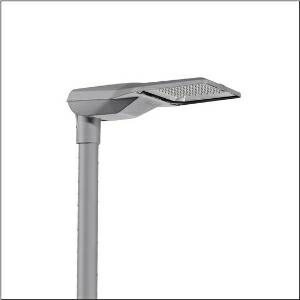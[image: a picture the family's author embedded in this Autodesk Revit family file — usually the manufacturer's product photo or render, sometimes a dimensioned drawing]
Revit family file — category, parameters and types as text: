
# Revit family: streetlight_sl_21_iq_midi___st1_5a_5xe3p41d08mb_62ad
name_source: partatom
category: Lighting Fixtures
units: mm (PartAtom-declared; Revit-internal decimal feet)

## family parameters
Cut with Voids When Loaded = No
Host = Face
Light Source = No
Part Type = Normal
Room Calculation Point = No
Round Connector Dimension = Use Diameter
Shared = No

## types (1)
- --- (1 x LED, 20000 lm, 146.7 W, 4000K)
    Apparent Load = 147 VA
    CIE Flux Codes = 22 53 95 100 100
    Color Rendering = 70
    Color Temperature = 4000K
    Default Elevation = 1800 mm
    Description = Streetlight SL 21 iQ midi, mast luminaire, primary light control with lens, of PMMA, primary optical cover: cover, of toughened safety glass, transparent, light distribution: ST1.5a, light emission: direct distribution, primary light characteristic: asymmetric, installation type: post-top, side-entry, LED, High Power LED, rated luminous flux: 20.000lm, luminous efficacy: 136lm/W, light colour: 740, colour temperature: 4000K, control gear: iQ-Comfort, control: Auto-Match, Temp-Guard, Lumen-Switch, Night-Set, Smart-Wire, Light-Fading, Desk-Remote (wireless, voltage-free reading and setting of iQ features in the workshop via application-optimized NFC function/RFID function), optimised constant luminous flux control (CLO 2.0), pre-setting: linear dimming characteristic, mains connection: 230..240V, AC, 50/60Hz, start of lifetime: 147W, end of service life: 161W, reduction: 62W, luminaire housing, of diecast aluminium, powder-coated, Siteco® metallic grey (DB 702S), corrosivity category C5 mid according to DIN EN ISO 12944, please order mast flange separately, inclination adjustable: 0°, 5°, 10°, 15°, sealing non-destructively replaceable, multi-level sealing system, length: 644mm, width: 335mm, height: 110mm, mast flange for spigot size: 42mm (side-entry): 5XC10008XM4, 60/48mm (side-entry/post-top): 5XC10108XM2, 76/60mm (side-entry/post-top): 5XC10108XM1, mounting height: 4..8m, protection rating (complete): IP66, insulation class (complete): insulation class II (safety insulation), certification: CE, ENEC, ENEC+, VDE, impact resistance: IK10, permissible operating ambient temperature for outdoor applications: -40..+50°C, standard-compliant lighting for roads and squares, packaging unit: 1 piece

Light Distribution: ST1.5a
    Height = 111 mm
    Lamp = 1 x LED
    Lamp Light Flux = 20000 lm
    Lamp Power = 146.7 W
    Lamp count = 1
    Length = 644 mm
    Luminous efficacy = 136 lm/W
    Manufacturer = Siteco
    ModVariant = No
    Model = 5XE3P41D08MB
    Number of Poles = 1
    OnlyDefault = Yes
    Power Factor = 1
    Product Name = Streetlight SL 21 iQ midi | ST1.5a
    Product group = mast luminaire | pylon top
    ProductGroupID = 6100
    Protection Class = Protection class II
    Protection Degree = IP 66
    RLX_Detail_Level = 1
    RLX_Emergency_Light_Flux = 0 lm
    RLX_Emergency_Type = 0
    RLX_Emergency_Type_DB = No
    RlxData = <blob elided: 30445 chars, md5=eae44379>
    Socket = socket
    Standby Power = 0 W
    System Light Flux = 20000 lm
    System Power = 147 W
    Type Comments = factory setting: luminous flux: 100 % | dim-lin: 254 | 753 mA
    Type Image = l_1004298.jpg
    URL = http://relux.com
    VarID = @adj_197723
    Voltage = 0 V
    Weight = 0.00 kg
    Width = 336 mm

## geometry (parser evidence)
native form markers: Blend x4, Sweep x11
no freeform markers — native parametric forms only
